# Revit family: Rectangular Pile Sheet Foundation
name_source: partatom
category: Structural Columns
units: mm (PartAtom-declared; Revit-internal decimal feet)

## family parameters
Always export as geometry = No
Beam cutback in plan = From geometry
Cut with Voids When Loaded = No
Display in Hidden Views = Edges Hidden by Other Members
Material for Model Behavior = Concrete
OmniClass Number = 23.25.30.11.14.11
OmniClass Title = Columns
Section Shape = Not Defined
Shared = No
Show family pre-cut in plan views = Yes

## types (4) — shared parameters
Center to center = 950 mm  [stored 3.1168 ft]
W = 943 mm

## per-type parameters (varying)
| type | Offset | b |
| 300mm | 200 mm  [stored 0.656168 ft] | 300 mm |
| 450mm | 263 mm | 450 mm  [stored 1.47638 ft] |
| 600mm | 263 mm | 600 mm |
| 750mm | 263 mm | 750 mm  [stored 2.46063 ft] |

note: [stored X ft] marks values corroborated as IEEE doubles in the binary element streams (Revit-internal decimal feet)

## geometry (parser evidence)
native form markers: Sweep x1
no freeform markers — native parametric forms only
